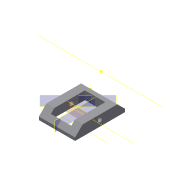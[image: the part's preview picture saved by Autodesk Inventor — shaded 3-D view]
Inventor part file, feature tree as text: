
AUTODESK INVENTOR PART (.ipt)
format: ipt  version: 2022 (Build 260153000, 153)  size: 250,368 bytes
history: native  units: mm
features: sketch x11, extrude x8, projected_geometry x7, plane x6, other x6, reference x3, hole x2, chamfer x1
ambient origin geometry x8: Origin, YZ Plane, XZ Plane, XY Plane, X Axis, Y Axis, Z Axis, Center Point
bodies: Volumenkörper1 (feature_tree)
feature tree (44):
  extrude  "Extrusion1"  Depth=28.0mm
  extrude  "Extrusion2"  Depth=1.4mm TaperAngle=0.0deg
  extrude  "Extrusion5"  Depth=16.5mm
  plane  "Arbeitsebene2"
  plane  "Arbeitsebene3"
  extrude  "Extrusion6"  Depth=6.0mm TaperAngle=0.0deg
  plane  "Arbeitsebene4"
  sketch  "Skizze7"  dims[d24=5.0mm d25=6.0mm d26=0.0mm]
  extrude  "Extrusion7"  Depth=5.0mm TaperAngle=0.0deg
  plane  "Arbeitsebene5"
  extrude  "Extrusion9"  Depth=3.0mm
  plane  "Arbeitsebene6"
  hole  "Bohrung3"  [1 undecoded]
  extrude  "Extrusion10"  Depth=2.0mm
  extrude  "Extrusion11"  Depth=10.0mm TaperAngle=0.0deg
  hole  "Bohrung2"  [1 undecoded]
  chamfer  "Fase3"  [1 undecoded]
  sketch  "Skizze1"  dims[d0=18.0mm d1=28.0mm]
  sketch  "Skizze2"  dims[d2=7.0mm d3=0.0mm d6=1.4mm d7=0.0mm]
  projected_geometry  "Projizierte Kontur4"
  sketch  "Skizze5"  dims[d16=25.5mm d17=16.5mm]
  projected_geometry  "Projizierte Kontur5"
  plane  "Arbeitsebene1"
  sketch  "Skizze6"  dims[d18=1.5mm d19=6.0mm d20=0.0mm]
  projected_geometry  "Projizierte Kontur6"
  sketch  "Skizze8"  dims[d27=3.0mm d28=3.0mm]
  projected_geometry  "Projizierte Kontur7"
  sketch  "Skizze10"  dims[d29=7.0mm d30=0.0mm d38=2.9mm]
  projected_geometry  "Projizierte Kontur8"
  sketch  "Skizze13"  dims[d39=0.0mm d40=0.0mm]
  sketch  "Skizze14"  dims[d48=4.0mm d49=6.0mm d50=4.0mm d51=2.0mm d52=90.0deg d53=0.1mm d54=20.594885mm d55=1.8mm]
  sketch  "Skizze15"  dims[d56=1.8mm d57=6.0mm d58=4.0mm d59=4.0mm d60=90.0deg d61=10.0mm d62=20.594885mm d63=4.0mm d64=0.0mm]
  projected_geometry  "Projizierte Kontur12"
  sketch  "Skizze16"  dims[d65=4.0mm d66=0.0mm d67=4.0mm d68=2.0mm d69=45.0deg]
  projected_geometry  "Projizierte Kontur13"
  reference  "Referenz1"
  reference  "Referenz2"
  reference  "Referenz4"
  other  "Assembly_Cube_Fibercombiner_v3.iam"
  other  "DIN 912 - ersetzt durch DIN EN ISO 4762 M3 x 25:3"
  other  "DIN 912 - ersetzt durch DIN EN ISO 4762 M3 x 25:1"
  other  "DIN 912 - ersetzt durch DIN EN ISO 4762 M3 x 25:2"
  other  "Assembly_Cube_empty_IM_v3:2"
  other  "10_Cube_1x1_IM:1"
note: 3 required parameter values undecoded (feature->parameter linkage not recoverable at this tier; creation-order binding heuristic only, values carry confidence <= 0.55)
